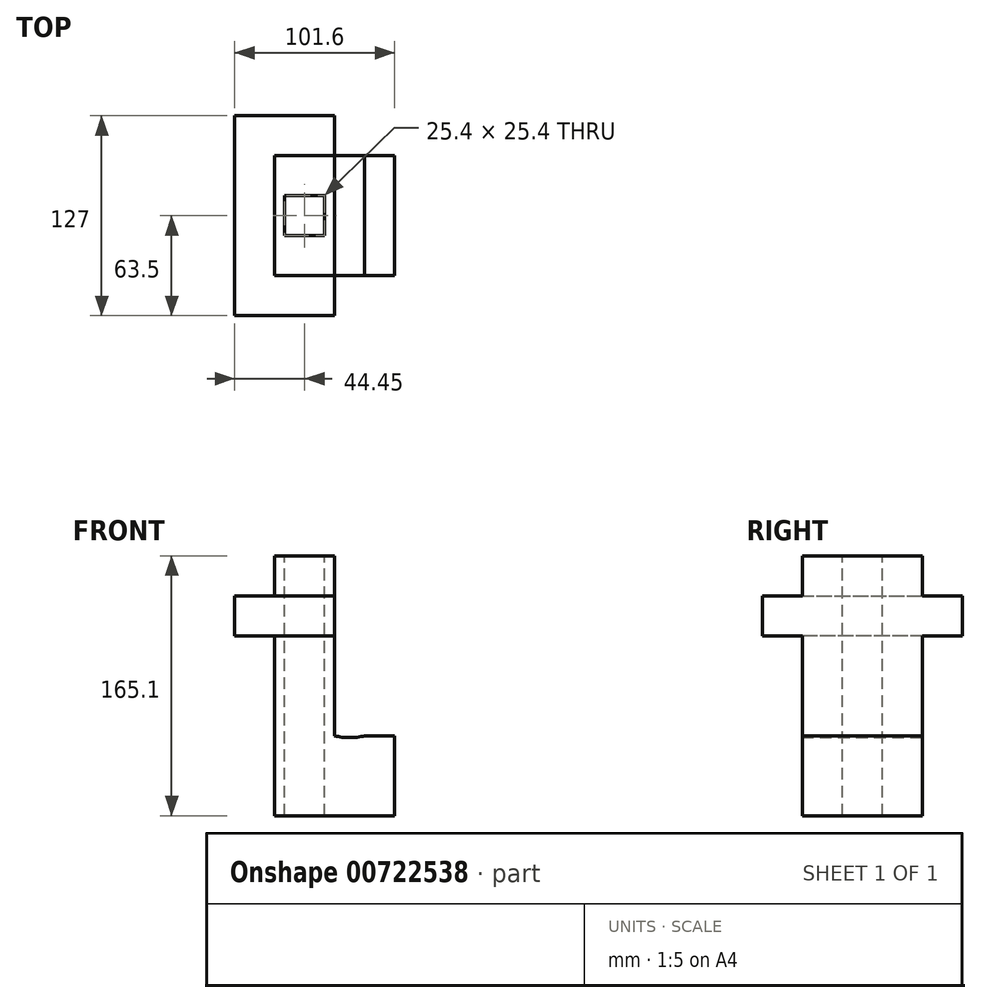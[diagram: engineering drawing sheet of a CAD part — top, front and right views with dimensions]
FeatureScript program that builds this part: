
annotation { "Feature Type Name" : "Feature", "Feature Type Description" : "" }
export const myFeature = defineFeature(function(context is Context, id is Id, definition is map)
    precondition{}
    {
        {
            var Q0;
            Q0=qCreatedBy(makeId("Top.planeOp"),FACE);
            var sketch = newSketch(context, id + "F0", { "sketchPlane" : qUnion([Q0])});
            skLineSegment(sketch, "E0.bottom", {"start": v(19.05, -38.1) * mm, "end": v(-19.05, -38.1) * mm});
            skLineSegment(sketch, "E0.top", {"start": v(19.05, 38.1) * mm, "end": v(-19.05, 38.1) * mm});
            skLineSegment(sketch, "E0.left", {"start": v(19.05, -38.1) * mm, "end": v(19.05, 38.1) * mm});
            skLineSegment(sketch, "E0.right", {"start": v(-19.05, -38.1) * mm, "end": v(-19.05, 38.1) * mm});
            skPoint(sketch, "E0.middle", {"position": v(0, 0) * mm});
            skSolve(sketch);
        }
        {
            var Q0;
            Q0=makeQuery(id+"F0.imprint","IMPRINT",FACE,{"disambiguationData":[TD([[makeQuery(id+"F0.imprint","IMPRINT",EDGE,{"derivedFrom":sQuery(id+"F0.wireOp",EDGE,"E0.bottom")}),-1.0]])]});
            extrude(context, id + "F1", {"entities" : qUnion([Q0]), "depth" : 177.8 * mm, "offsetDistance" : 25.4 * mm});
        }
        {
            var Q0;
            Q0=makeQuery(id+"F1.opExtrude","SWEPT_FACE",FACE,{"disambiguationData":[OSD([sQuery(id+"F0.wireOp",EDGE,"E0.right")])]});
            var sketch = newSketch(context, id + "F2", { "sketchPlane" : qUnion([Q0])});
            skLineSegment(sketch, "E1", {"start": v(38.1, 139.7) * mm, "end": v(-38.1, 139.7) * mm});
            skLineSegment(sketch, "E2", {"start": v(-38.1, 139.7) * mm, "end": v(-38.1, 114.3) * mm});
            skLineSegment(sketch, "E3", {"start": v(-38.1, 114.3) * mm, "end": v(38.1, 114.3) * mm});
            skLineSegment(sketch, "E4", {"start": v(38.1, 114.3) * mm, "end": v(38.1, 139.7) * mm});
            skSolve(sketch);
        }
        {
            var Q0;
            Q0=makeQuery(id+"F2.imprint","IMPRINT",FACE,{"disambiguationData":[TD([[makeQuery(id+"F2.imprint","IMPRINT",EDGE,{"derivedFrom":sQuery(id+"F2.wireOp",EDGE,"E1")}),1.0]])]});
            extrude(context, id + "F3", {"entities" : qUnion([Q0]), "operationType" : NewBodyOperationType.ADD, "depth" : 25.4 * mm, "offsetDistance" : 25.4 * mm});
        }
        {
            var Q0;
            Q0=makeQuery(id+"F3.boolean.opBoolean","MERGE",FACE,{"derivedFrom":[makeQuery(id+"F1.opExtrude","SWEPT_FACE",FACE,{"disambiguationData":[OSD([sQuery(id+"F0.wireOp",EDGE,"E0.bottom")])]}),makeQuery(id+"F3.opExtrude","SWEPT_FACE",FACE,{"disambiguationData":[OSD([sQuery(id+"F2.wireOp",EDGE,"E4")])]})]});
            var sketch = newSketch(context, id + "F4", { "sketchPlane" : qUnion([Q0])});
            skLineSegment(sketch, "E5", {"start": v(-63.5, 114.3) * mm, "end": v(19.05, 114.3) * mm});
            skLineSegment(sketch, "E6", {"start": v(19.05, 114.3) * mm, "end": v(19.05, 139.7) * mm});
            skLineSegment(sketch, "E7", {"start": v(19.05, 139.7) * mm, "end": v(-44.45, 139.7) * mm});
            skSolve(sketch);
        }
        {
            var Q0;
            {var subQ11=sQuery(id+"F4.wireOp",EDGE,"E6");Q0=makeQuery(id+"F4.imprint","IMPRINT",FACE,{"disambiguationData":[TD([[makeQuery(id+"F4.imprint","IMPRINT",EDGE,{"derivedFrom":subQ11}),-1.0]])]});}
            extrude(context, id + "F5", {"entities" : qUnion([Q0]), "operationType" : NewBodyOperationType.ADD, "depth" : 25.4 * mm, "offsetDistance" : 25.4 * mm});
        }
        {
            var Q0;
            Q0=makeQuery(id+"F3.boolean.opBoolean","MERGE",FACE,{"derivedFrom":[makeQuery(id+"F1.opExtrude","SWEPT_FACE",FACE,{"disambiguationData":[OSD([sQuery(id+"F0.wireOp",EDGE,"E0.top")])]}),makeQuery(id+"F3.opExtrude","SWEPT_FACE",FACE,{"disambiguationData":[OSD([sQuery(id+"F2.wireOp",EDGE,"E2")])]})]});
            var sketch = newSketch(context, id + "F6", { "sketchPlane" : qUnion([Q0])});
            skLineSegment(sketch, "E8", {"start": v(44.45, 139.7) * mm, "end": v(-19.05, 139.7) * mm});
            skLineSegment(sketch, "E9", {"start": v(-19.05, 139.7) * mm, "end": v(-19.05, 114.3) * mm});
            skLineSegment(sketch, "E10", {"start": v(-19.05, 114.3) * mm, "end": v(44.45, 114.3) * mm});
            skSolve(sketch);
        }
        {
            var Q0;
            Q0=qSketchRegion(id+"F6",true);
            var Q1;
            {var subQ11=sQuery(id+"F6.wireOp",EDGE,"E9");Q1=makeQuery(id+"F6.imprint","IMPRINT",FACE,{"disambiguationData":[TD([[makeQuery(id+"F6.imprint","IMPRINT",EDGE,{"derivedFrom":subQ11}),1.0]])]});}
            extrude(context, id + "F7", {"entities" : qUnion([Q0, Q1]), "operationType" : NewBodyOperationType.ADD, "depth" : 25.4 * mm, "offsetDistance" : 25.4 * mm});
        }
        {
            var Q0;
            Q0=makeQuery(id+"F7.boolean.opBoolean","MERGE",FACE,{"derivedFrom":[makeQuery(id+"F5.boolean.opBoolean","MERGE",FACE,{"derivedFrom":[makeQuery(id+"F1.opExtrude","SWEPT_FACE",FACE,{"disambiguationData":[OSD([sQuery(id+"F0.wireOp",EDGE,"E0.left")])]}),makeQuery(id+"F5.opExtrude","SWEPT_FACE",FACE,{"disambiguationData":[OSD([sQuery(id+"F4.wireOp",EDGE,"E6")])]})]}),makeQuery(id+"F7.opExtrude","SWEPT_FACE",FACE,{"disambiguationData":[OSD([sQuery(id+"F6.wireOp",EDGE,"E9")])]})]});
            var sketch = newSketch(context, id + "F8", { "sketchPlane" : qUnion([Q0])});
            skLineSegment(sketch, "E11", {"start": v(-63.5, 139.7) * mm, "end": v(-63.5, 137.16) * mm});
            skLineSegment(sketch, "E12", {"start": v(-63.5, 137.16) * mm, "end": v(-38.1, 114.3) * mm});
            skLineSegment(sketch, "E13", {"start": v(63.5, 139.7) * mm, "end": v(63.5, 137.16) * mm});
            skLineSegment(sketch, "E14", {"start": v(63.5, 137.16) * mm, "end": v(38.1, 114.3) * mm});
            skSolve(sketch);
        }
        {
            var Q0;
            Q0=makeQuery(id+"F1.opExtrude","CAP_FACE",FACE,{"disambiguationData":[OSD([sQuery(id+"F0.wireOp",EDGE,"E0.bottom"),sQuery(id+"F0.wireOp",EDGE,"E0.top"),sQuery(id+"F0.wireOp",EDGE,"E0.left"),sQuery(id+"F0.wireOp",EDGE,"E0.right")])],"isStart":false});
            var sketch = newSketch(context, id + "F9", { "sketchPlane" : qUnion([Q0])});
            skLineSegment(sketch, "E15.bottom", {"start": v(-19.05, 38.1) * mm, "end": v(19.05, 38.1) * mm});
            skLineSegment(sketch, "E15.top", {"start": v(-19.05, -38.1) * mm, "end": v(19.05, -38.1) * mm});
            skLineSegment(sketch, "E15.left", {"start": v(-19.05, 38.1) * mm, "end": v(-19.05, -38.1) * mm});
            skLineSegment(sketch, "E15.right", {"start": v(19.05, 38.1) * mm, "end": v(19.05, -38.1) * mm});
            skSolve(sketch);
        }
        {
            var Q0;
            Q0=makeQuery(id+"F9.imprint","IMPRINT",FACE,{"disambiguationData":[TD([[makeQuery(id+"F9.imprint","IMPRINT",EDGE,{"derivedFrom":sQuery(id+"F9.wireOp",EDGE,"E15.bottom")}),1.0]])]});
            extrude(context, id + "F10", {"entities" : qUnion([Q0]), "operationType" : NewBodyOperationType.ADD, "depth" : 25.4 * mm, "offsetDistance" : 25.4 * mm});
        }
        {
            var Q0;
            Q0=makeQuery(id+"F10.opExtrude","CAP_FACE",FACE,{"disambiguationData":[OSD([sQuery(id+"F9.wireOp",EDGE,"E15.bottom"),sQuery(id+"F9.wireOp",EDGE,"E15.top"),sQuery(id+"F9.wireOp",EDGE,"E15.left"),sQuery(id+"F9.wireOp",EDGE,"E15.right")])],"isStart":false});
            var sketch = newSketch(context, id + "F11", { "sketchPlane" : qUnion([Q0])});
            skLineSegment(sketch, "E16", {"start": v(-12.7, 12.7) * mm, "end": v(-12.7, -12.7) * mm});
            skLineSegment(sketch, "E17", {"start": v(-12.7, -12.7) * mm, "end": v(12.7, -12.7) * mm});
            skLineSegment(sketch, "E18", {"start": v(12.7, -12.7) * mm, "end": v(12.7, 12.7) * mm});
            skLineSegment(sketch, "E19", {"start": v(12.7, 12.7) * mm, "end": v(-12.7, 12.7) * mm});
            skSolve(sketch);
        }
        {
            var Q0;
            Q0=qSketchRegion(id+"F11",true);
            extrude(context, id + "F12", {"entities" : qUnion([Q0]), "operationType" : NewBodyOperationType.REMOVE, "oppositeDirection" : true, "depth" : 228.6 * mm, "offsetDistance" : 25.4 * mm});
        }
        {
            var Q0;
            Q0=makeQuery(id+"F10.boolean.opBoolean","MERGE",FACE,{"derivedFrom":[makeQuery(id+"F7.boolean.opBoolean","MERGE",FACE,{"derivedFrom":[makeQuery(id+"F5.boolean.opBoolean","MERGE",FACE,{"derivedFrom":[makeQuery(id+"F1.opExtrude","SWEPT_FACE",FACE,{"disambiguationData":[OSD([sQuery(id+"F0.wireOp",EDGE,"E0.left")])]}),makeQuery(id+"F5.opExtrude","SWEPT_FACE",FACE,{"disambiguationData":[OSD([sQuery(id+"F4.wireOp",EDGE,"E6")])]})]}),makeQuery(id+"F7.opExtrude","SWEPT_FACE",FACE,{"disambiguationData":[OSD([sQuery(id+"F6.wireOp",EDGE,"E9")])]})]}),makeQuery(id+"F10.opExtrude","SWEPT_FACE",FACE,{"disambiguationData":[OSD([sQuery(id+"F9.wireOp",EDGE,"E15.right")])]})]});
            var sketch = newSketch(context, id + "F13", { "sketchPlane" : qUnion([Q0])});
            skLineSegment(sketch, "E20", {"start": v(-38.1, 0) * mm, "end": v(-38.1, 50.8) * mm});
            skLineSegment(sketch, "E21", {"start": v(-38.1, 50.8) * mm, "end": v(38.1, 50.8) * mm});
            skLineSegment(sketch, "E22", {"start": v(38.1, 50.8) * mm, "end": v(38.1, 0) * mm});
            skLineSegment(sketch, "E23", {"start": v(38.1, 0) * mm, "end": v(-38.1, 0) * mm});
            skSolve(sketch);
        }
        {
            var Q0;
            Q0=makeQuery(id+"F13.imprint","IMPRINT",FACE,{"disambiguationData":[TD([[makeQuery(id+"F13.imprint","IMPRINT",EDGE,{"derivedFrom":sQuery(id+"F13.wireOp",EDGE,"E20")}),1.0]])]});
            extrude(context, id + "F14", {"entities" : qUnion([Q0]), "operationType" : NewBodyOperationType.ADD, "depth" : 38.1 * mm, "offsetDistance" : 25.4 * mm});
        }
        {
            var Q0;
            {var subQ2=sQuery(id+"F0.wireOp",EDGE,"E0.bottom");Q0=makeQuery(id+"F14.boolean.opBoolean","MERGE",FACE,{"derivedFrom":[makeQuery(id+"F5.boolean.opBoolean","SPLIT",FACE,{"disambiguationData":[TD([makeQuery(id+"F3.opExtrude","SWEPT_FACE",FACE,{"disambiguationData":[OSD([sQuery(id+"F2.wireOp",EDGE,"E3")])]})])],"derivedFrom":makeQuery(id+"F3.boolean.opBoolean","MERGE",FACE,{"derivedFrom":[makeQuery(id+"F1.opExtrude","SWEPT_FACE",FACE,{"disambiguationData":[OSD([subQ2])]}),makeQuery(id+"F3.opExtrude","SWEPT_FACE",FACE,{"disambiguationData":[OSD([sQuery(id+"F2.wireOp",EDGE,"E4")])]})]})}),makeQuery(id+"F14.opExtrude","SWEPT_FACE",FACE,{"disambiguationData":[OSD([sQuery(id+"F13.wireOp",EDGE,"E20")])]})]});}
            var sketch = newSketch(context, id + "F15", { "sketchPlane" : qUnion([Q0])});
            skArc(sketch, "E24", {"start": v(19.05, 50.8) * mm, "mid": v(28.58, 49.6) * mm, "end": v(38.1, 50.8) * mm});
            skSolve(sketch);
        }
        {
            var Q0;
            {var subQ0=sQuery(id+"F15.wireOp",EDGE,"E24");Q0=makeQuery(id+"F15.imprint","IMPRINT",FACE,{"disambiguationData":[TD([[makeQuery(id+"F15.imprint","IMPRINT",EDGE,{"derivedFrom":subQ0}),1.0]])]});}
            extrude(context, id + "F16", {"entities" : qUnion([Q0]), "operationType" : NewBodyOperationType.REMOVE, "oppositeDirection" : true, "depth" : 228.6 * mm, "offsetDistance" : 25.4 * mm});
        }
        {
            var Q0;
            Q0=makeQuery(id+"F10.opExtrude","CAP_FACE",FACE,{"disambiguationData":[OSD([sQuery(id+"F9.wireOp",EDGE,"E15.bottom"),sQuery(id+"F9.wireOp",EDGE,"E15.top"),sQuery(id+"F9.wireOp",EDGE,"E15.left"),sQuery(id+"F9.wireOp",EDGE,"E15.right")])],"isStart":false});
            var sketch = newSketch(context, id + "F17", { "sketchPlane" : qUnion([Q0])});
            skLineSegment(sketch, "E25", {"start": v(-19.05, 38.1) * mm, "end": v(19.05, 38.1) * mm});
            skLineSegment(sketch, "E26", {"start": v(19.05, 38.1) * mm, "end": v(19.05, -38.1) * mm});
            skLineSegment(sketch, "E27", {"start": v(19.05, -38.1) * mm, "end": v(-19.05, -38.1) * mm});
            skLineSegment(sketch, "E28", {"start": v(-19.05, -38.1) * mm, "end": v(-19.05, 38.1) * mm});
            skSolve(sketch);
        }
        {
            var Q0;
            Q0=makeQuery(id+"F17.imprint","IMPRINT",FACE,{"disambiguationData":[TD([[makeQuery(id+"F17.imprint","IMPRINT",EDGE,{"derivedFrom":sQuery(id+"F17.wireOp",EDGE,"E25")}),1.0]])]});
            extrude(context, id + "F18", {"entities" : qUnion([Q0]), "operationType" : NewBodyOperationType.REMOVE, "oppositeDirection" : true, "depth" : 38.1 * mm, "offsetDistance" : 25.4 * mm});
        }
    });
